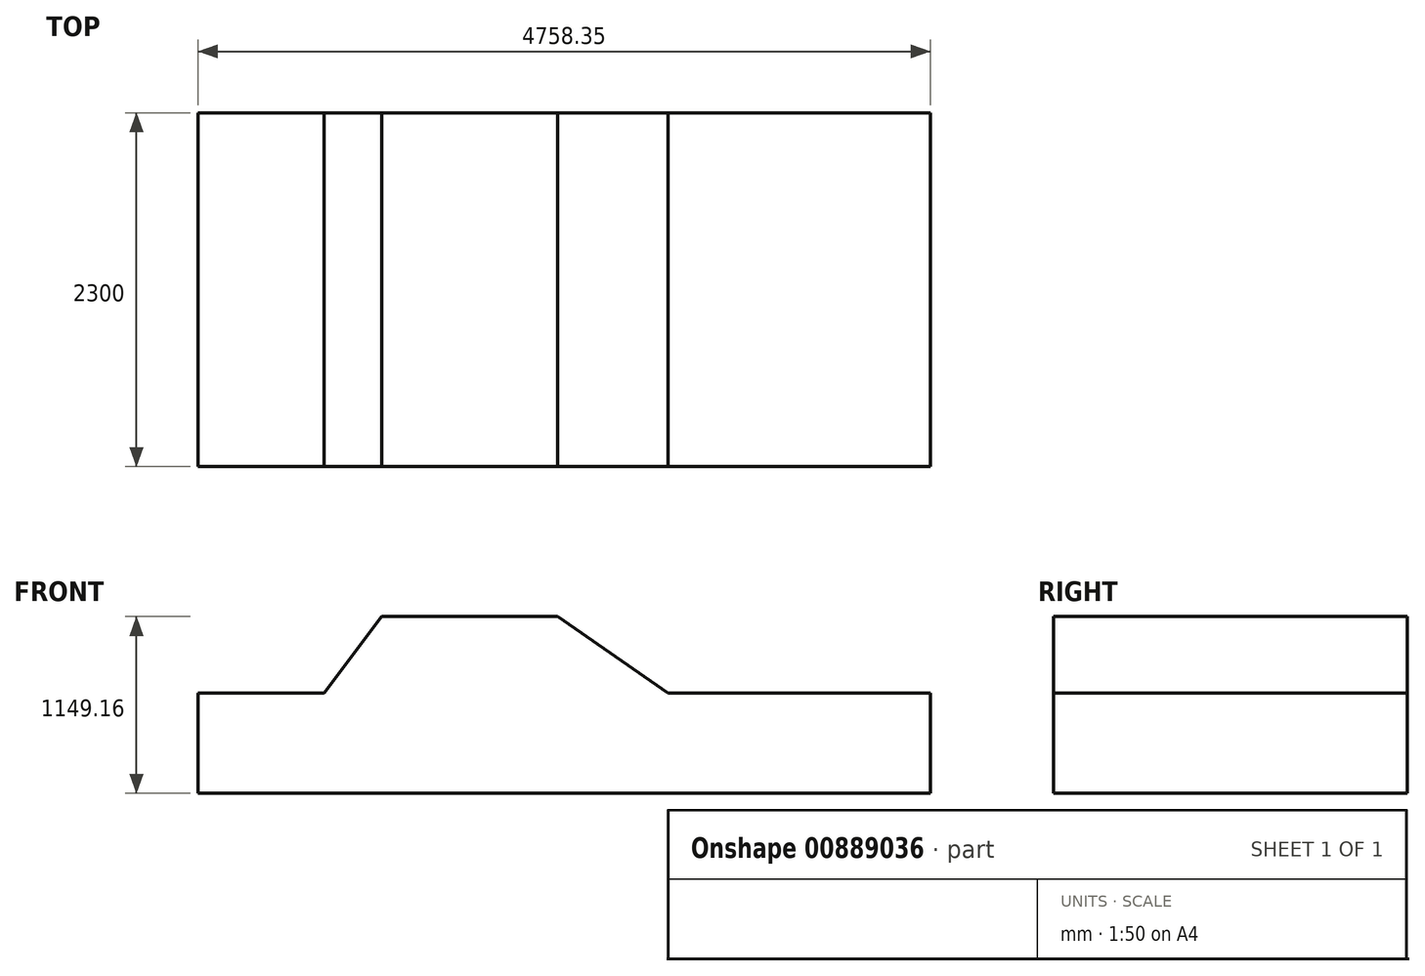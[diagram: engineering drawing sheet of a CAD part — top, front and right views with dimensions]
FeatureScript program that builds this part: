
annotation { "Feature Type Name" : "Feature", "Feature Type Description" : "" }
export const myFeature = defineFeature(function(context is Context, id is Id, definition is map)
    precondition{}
    {
        {
            var Q0;
            Q0=qCreatedBy(makeId("Front.planeOp"),FACE);
            var sketch = newSketch(context, id + "F0", { "sketchPlane" : qUnion([Q0])});
            skLineSegment(sketch, "E0", {"start": v(-1732.43, 0) * mm, "end": v(3025.92, 0) * mm});
            skLineSegment(sketch, "E1", {"start": v(3025.92, 0) * mm, "end": v(3025.92, 652.4) * mm});
            skLineSegment(sketch, "E2", {"start": v(3025.92, 652.4) * mm, "end": v(1319.91, 652.4) * mm});
            skLineSegment(sketch, "E3", {"start": v(1319.91, 652.4) * mm, "end": v(603.17, 1149.16) * mm});
            skLineSegment(sketch, "E4", {"start": v(603.17, 1149.16) * mm, "end": v(-538.48, 1149.16) * mm});
            skLineSegment(sketch, "E5", {"start": v(-538.48, 1149.16) * mm, "end": v(-914.6, 652.4) * mm});
            skLineSegment(sketch, "E6", {"start": v(-914.6, 652.4) * mm, "end": v(-1732.43, 652.4) * mm});
            skLineSegment(sketch, "E7", {"start": v(-1732.43, 652.4) * mm, "end": v(-1732.43, 0) * mm});
            skLineSegment(sketch, "E8", {"start": v(-1732.43, 0) * mm, "end": v(-1732.43, 280.28) * mm});
            skLineSegment(sketch, "E9", {"start": v(-1732.43, 280.28) * mm, "end": v(3025.92, 280.28) * mm});
            skLineSegment(sketch, "E10", {"start": v(3025.92, 280.28) * mm, "end": v(2706.87, 280.28) * mm});
            skLineSegment(sketch, "E11", {"start": v(2706.87, 280.28) * mm, "end": v(2393.77, 280.28) * mm});
            skLineSegment(sketch, "E12", {"start": v(2393.77, 280.28) * mm, "end": v(-810.5, 280.28) * mm});
            skLineSegment(sketch, "E13", {"start": v(-810.5, 280.28) * mm, "end": v(-1123.6, 280.28) * mm});
            skLineSegment(sketch, "E14", {"start": v(-1123.6, 280.28) * mm, "end": v(-1732.43, 280.28) * mm});
            skLineSegment(sketch, "E15", {"start": v(3025.92, 0) * mm, "end": v(2706.87, 0) * mm});
            skLineSegment(sketch, "E16", {"start": v(2706.87, 0) * mm, "end": v(2393.77, 0) * mm});
            skLineSegment(sketch, "E17", {"start": v(2393.77, 0) * mm, "end": v(-810.5, 0) * mm});
            skLineSegment(sketch, "E18", {"start": v(-810.5, 0) * mm, "end": v(-1123.6, 0) * mm});
            skLineSegment(sketch, "E19", {"start": v(-1123.6, 0) * mm, "end": v(-1732.43, 0) * mm});
            skSolve(sketch);
        }
        {
            var Q0;
            Q0 = qSketchRegion(id + "F0", true);
            extrude(context, id + "F1", {"entities" : qUnion([Q0]), "depth" : 2300 * mm, "offsetDistance" : 25 * mm});
        }
    });
